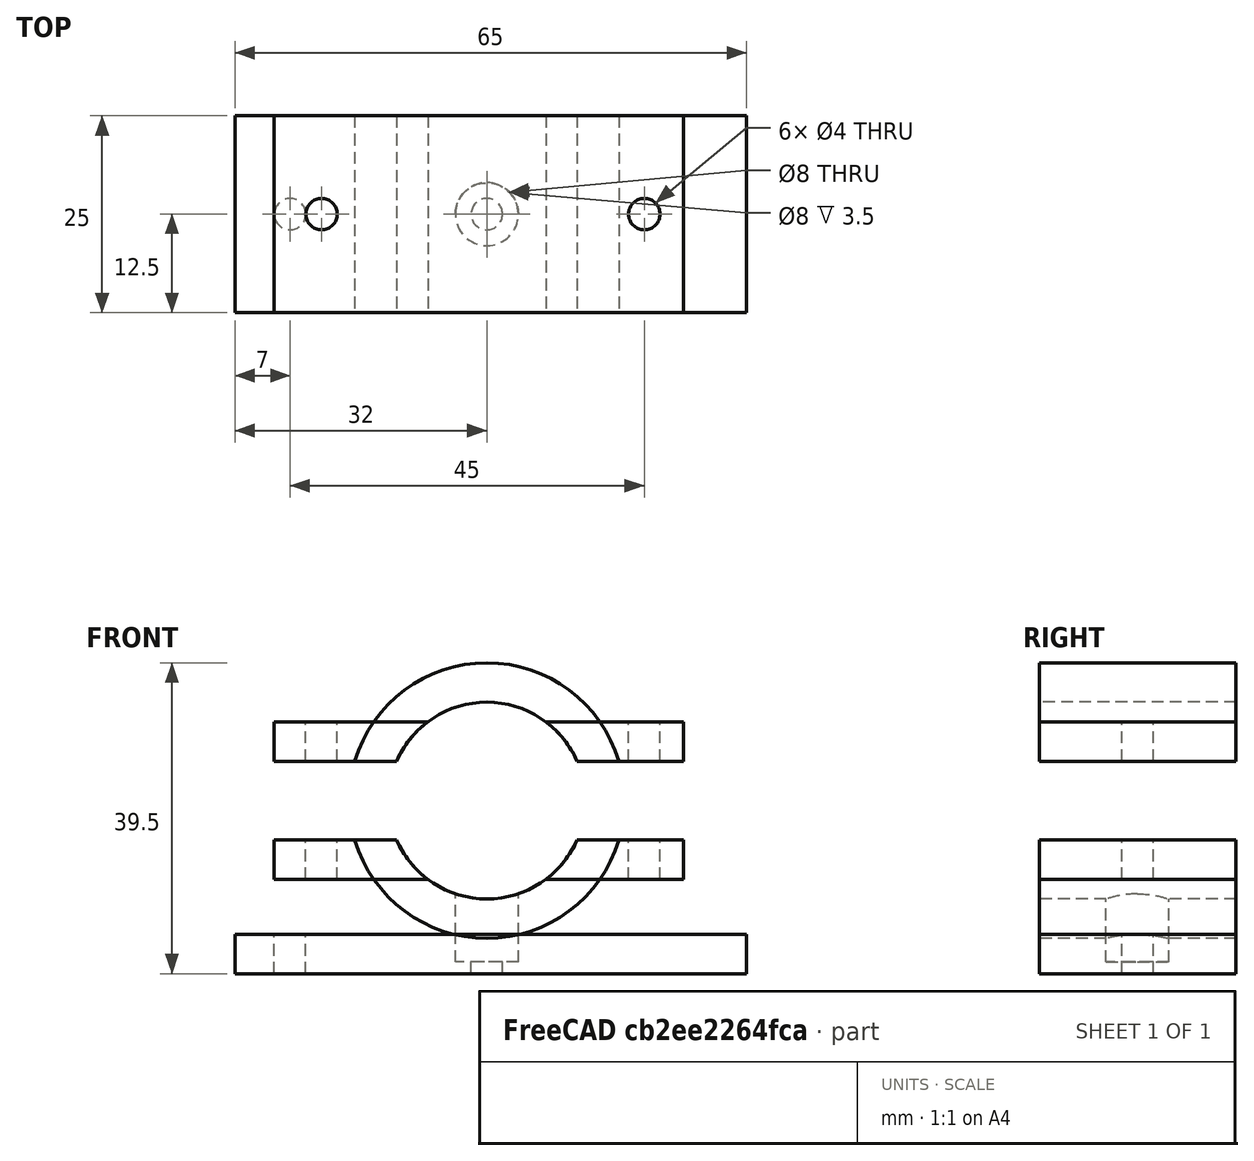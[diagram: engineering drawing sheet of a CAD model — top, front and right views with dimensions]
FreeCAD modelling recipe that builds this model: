
FCSTD DOCUMENT  (FreeCAD 0.16R)
Label: soportebiciAirBeam
License: All rights reserved
LicenseURL: http://en.wikipedia.org/wiki/All_rights_reserved
objects: Part::Cylinder×14, Part::Cut×14, Part::Box×4
note: 32 computed .brp shape members not serialized (recipe doc carries the construction recipe); baked Part::Feature solids carry a one-line shape summary decoded from their .brp

FEATURE [Part::Box] Box  label="Cubo"
  Height = 5
  Length = 65
  Width = 25
FEATURE [Part::Cylinder] Cylinder  label="Cilindro"
  Angle = 360
  Height = 10
  Placement = pos=(7,12.5,0) rot=(0,0,1;0rad)
  Radius = 2
FEATURE [Part::Cylinder] Cylinder001  label="Cilindro001"
  Angle = 360
  Height = 10
  Placement = pos=(32,12.5,0) rot=(0,0,1;0rad)
  Radius = 2
FEATURE [Part::Cylinder] Cylinder002  label="Cilindro002"
  Angle = 360
  Height = 12
  Placement = pos=(32,12.5,3) rot=(0,0,1;0rad)
  Radius = 3
FEATURE [Part::Cylinder] Cylinder003  label="Cilindro003"
  Angle = 360
  Height = 25
  Placement = pos=(32,25,22) rot=(1,0,0;1.5708rad)
  Radius = 12.5
FEATURE [Part::Cylinder] Cylinder004  label="Cilindro004"
  Angle = 360
  Height = 25
  Placement = pos=(32,25,22) rot=(1,0,0;1.5708rad)
  Radius = 17.5
FEATURE [Part::Cut] Cut
  Base = -> Cylinder004
  Tool = -> Cylinder003
FEATURE [Part::Box] Box001  label="Cubo001"
  Height = 10
  Length = 65
  Placement = pos=(0,0,17) rot=(0,0,1;0rad)
  Width = 25
FEATURE [Part::Cut] Cut001
  Base = -> Cut
  Tool = -> Box001
FEATURE [Part::Cut] Cut002
  Base = -> Box
  Tool = -> Cylinder
FEATURE [Part::Box] Box002  label="Cubo002"
  Height = 5
  Length = 52
  Placement = pos=(5,0,27) rot=(0,0,1;0rad)
  Width = 25
FEATURE [Part::Box] Box003  label="Cubo003"
  Height = 5
  Length = 52
  Placement = pos=(5,0,12) rot=(0,0,1;0rad)
  Width = 25
FEATURE [Part::Cylinder] Cylinder005  label="Cilindro005"
  Angle = 360
  Height = 25
  Placement = pos=(32,25,22) rot=(1,0,0;1.5708rad)
  Radius = 12.5
FEATURE [Part::Cylinder] Cylinder006  label="Cilindro006"
  Angle = 360
  Height = 25
  Placement = pos=(32,25,22) rot=(1,0,0;1.5708rad)
  Radius = 12.5
FEATURE [Part::Cut] Cut003
  Base = -> Box002
  Tool = -> Cylinder005
FEATURE [Part::Cut] Cut004
  Base = -> Box003
  Tool = -> Cylinder006
FEATURE [Part::Cylinder] Cylinder007  label="Cilindro007"
  Angle = 360
  Height = 30
  Placement = pos=(11,12.5,7) rot=(0,0,1;0rad)
  Radius = 2
FEATURE [Part::Cylinder] Cylinder008  label="Cilindro008"
  Angle = 360
  Height = 30
  Placement = pos=(52,12.5,7) rot=(0,0,1;0rad)
  Radius = 2
FEATURE [Part::Cylinder] Cylinder009  label="Cilindro009"
  Angle = 360
  Height = 30
  Placement = pos=(11,12.5,7) rot=(0,0,1;0rad)
  Radius = 2
FEATURE [Part::Cut] Cut005
  Base = -> Cut003
  Tool = -> Cylinder009
FEATURE [Part::Cut] Cut006
  Base = -> Cut004
  Tool = -> Cylinder007
FEATURE [Part::Cylinder] Cylinder010  label="Cilindro010"
  Angle = 360
  Height = 30
  Placement = pos=(52,12.5,7) rot=(0,0,1;0rad)
  Radius = 2
FEATURE [Part::Cut] Cut007
  Base = -> Cut005
  Tool = -> Cylinder008
FEATURE [Part::Cut] Cut008
  Base = -> Cut006
  Tool = -> Cylinder010
FEATURE [Part::Cylinder] Cylinder011  label="Cilindro011"
  Angle = 360
  Height = 12
  Placement = pos=(32,12.5,3) rot=(0,0,1;0rad)
  Radius = 3
FEATURE [Part::Cut] Cut009
  Base = -> Cut001
  Tool = -> Cylinder011
FEATURE [Part::Cut] Cut010
  Base = -> Cut002
  Tool = -> Cylinder002
FEATURE [Part::Cut] Cut011
  Base = -> Cut010
  Tool = -> Cylinder001
FEATURE [Part::Cylinder] Cylinder013  label="Cilindro013"
  Angle = 360
  Height = 12
  Placement = pos=(32,12.5,1.5) rot=(0,0,1;0rad)
  Radius = 4
FEATURE [Part::Cylinder] Cylinder014  label="Cilindro014"
  Angle = 360
  Height = 12
  Placement = pos=(32,12.5,1.5) rot=(0,0,1;0rad)
  Radius = 4
FEATURE [Part::Cut] Cut012
  Base = -> Cut009
  Tool = -> Cylinder014
FEATURE [Part::Cut] Cut013
  Base = -> Cut011
  Tool = -> Cylinder013
